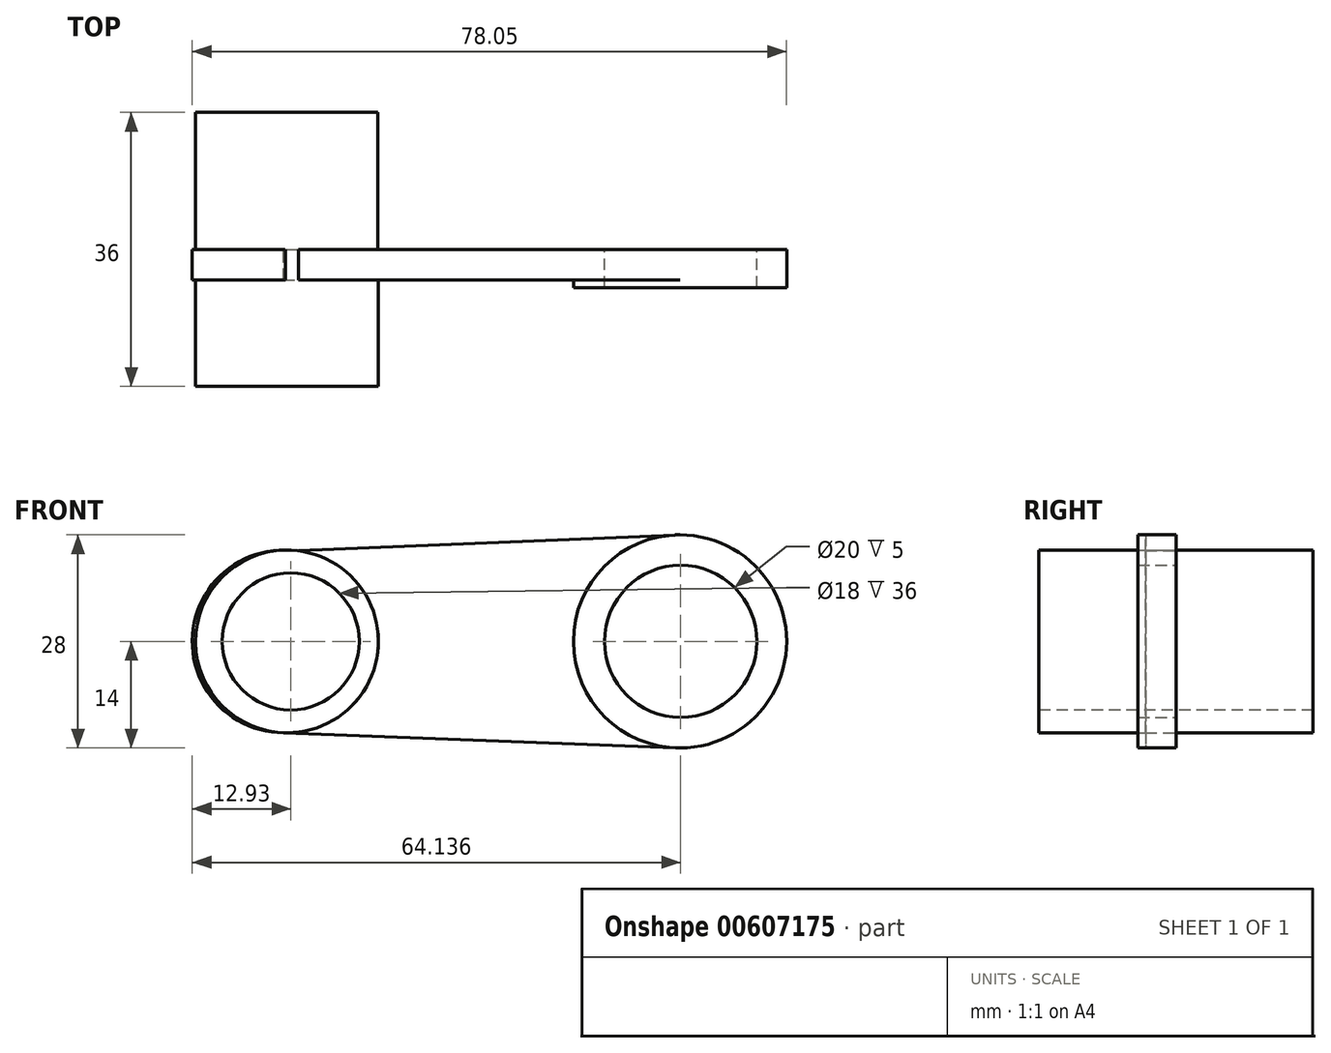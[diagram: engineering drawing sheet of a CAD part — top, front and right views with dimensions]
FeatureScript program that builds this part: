
annotation { "Feature Type Name" : "Feature", "Feature Type Description" : "" }
export const myFeature = defineFeature(function(context is Context, id is Id, definition is map)
    precondition{}
    {
        {
            var Q0;
            Q0=qCreatedBy(makeId("Front.planeOp"),FACE);
            var sketch = newSketch(context, id + "F0", { "sketchPlane" : qUnion([Q0])});
            skArc(sketch, "E0", {"start": v(-23.04, 11.89) * mm, "mid": v(-36.65, 0.82) * mm, "end": v(-24.67, -12) * mm});
            skArc(sketch, "E1", {"start": v(26.78, -13.99) * mm, "mid": v(41.33, 0.02) * mm, "end": v(26.74, 13.99) * mm});
            skLineSegment(sketch, "E2", {"start": v(-23.04, 11.89) * mm, "end": v(26.74, 13.99) * mm});
            skLineSegment(sketch, "E3", {"start": v(-24.67, -12) * mm, "end": v(26.78, -13.99) * mm});
            skSolve(sketch);
        }
        {
            var Q0;
            Q0 = qSketchRegion(id + "F0", true);
            extrude(context, id + "F1", {"entities" : qUnion([Q0]), "depth" : 4 * mm, "offsetDistance" : 25 * mm});
        }
        {
            var Q0;
            Q0=qCreatedBy(makeId("Front.planeOp"),FACE);
            var sketch = newSketch(context, id + "F2", { "sketchPlane" : qUnion([Q0])});
            skCircle(sketch, "E4", {"center": v(-24.23, 0) * mm, "radius": 12 * mm});
            skSolve(sketch);
        }
        {
            var Q0;
            Q0 = qSketchRegion(id + "F2", true);
            extrude(context, id + "F3", {"entities" : qUnion([Q0]), "operationType" : NewBodyOperationType.ADD, "depth" : 18 * mm, "offsetDistance" : 25 * mm});
        }
        {
            var Q0;
            Q0=qCreatedBy(makeId("Front.planeOp"),FACE);
            var sketch = newSketch(context, id + "F4", { "sketchPlane" : qUnion([Q0])});
            skCircle(sketch, "E5", {"center": v(-24.28, 0) * mm, "radius": 12 * mm});
            skSolve(sketch);
        }
        {
            var Q0;
            Q0 = qSketchRegion(id + "F4", true);
            var Q1;
            Q1=makeQuery(id+"F4.imprint","IMPRINT",FACE,{"disambiguationData":[TD([[makeQuery(id+"F4.imprint","IMPRINT",EDGE,{"derivedFrom":sQuery(id+"F4.wireOp",EDGE,"E5")}),1.0]])]});
            extrude(context, id + "F5", {"entities" : qUnion([Q0, Q1]), "operationType" : NewBodyOperationType.ADD, "oppositeDirection" : true, "depth" : 18 * mm, "offsetDistance" : 25 * mm});
        }
        {
            var Q0;
            Q0=qCreatedBy(makeId("Front.planeOp"),FACE);
            var sketch = newSketch(context, id + "F6", { "sketchPlane" : qUnion([Q0])});
            skCircle(sketch, "E6", {"center": v(27.38, 0) * mm, "radius": 14 * mm});
            skSolve(sketch);
        }
        {
            var Q0;
            Q0 = qSketchRegion(id + "F6", true);
            extrude(context, id + "F7", {"entities" : qUnion([Q0]), "operationType" : NewBodyOperationType.ADD, "depth" : 5 * mm, "offsetDistance" : 25 * mm});
        }
        {
            var Q0;
            Q0=qCreatedBy(makeId("Front.planeOp"),FACE);
            var sketch = newSketch(context, id + "F8", { "sketchPlane" : qUnion([Q0])});
            skCircle(sketch, "E7", {"center": v(27.47, 0) * mm, "radius": 10 * mm});
            skSolve(sketch);
        }
        {
            var Q0;
            Q0 = qSketchRegion(id + "F8", true);
            extrude(context, id + "F9", {"entities" : qUnion([Q0]), "operationType" : NewBodyOperationType.REMOVE, "depth" : 25 * mm, "offsetDistance" : 25 * mm});
        }
        {
            var Q0;
            Q0=qCreatedBy(makeId("Front.planeOp"),FACE);
            var sketch = newSketch(context, id + "F10", { "sketchPlane" : qUnion([Q0])});
            skCircle(sketch, "E8", {"center": v(-23.74, 0) * mm, "radius": 9 * mm});
            skSolve(sketch);
        }
        {
            var Q0;
            Q0 = qSketchRegion(id + "F10", true);
            extrude(context, id + "F11", {"entities" : qUnion([Q0]), "operationType" : NewBodyOperationType.REMOVE, "oppositeDirection" : true, "depth" : 25 * mm, "offsetDistance" : 25 * mm, "hasSecondDirection" : true, "secondDirectionOppositeDirection" : false, "secondDirectionDepth" : 25 * mm});
        }
    });
